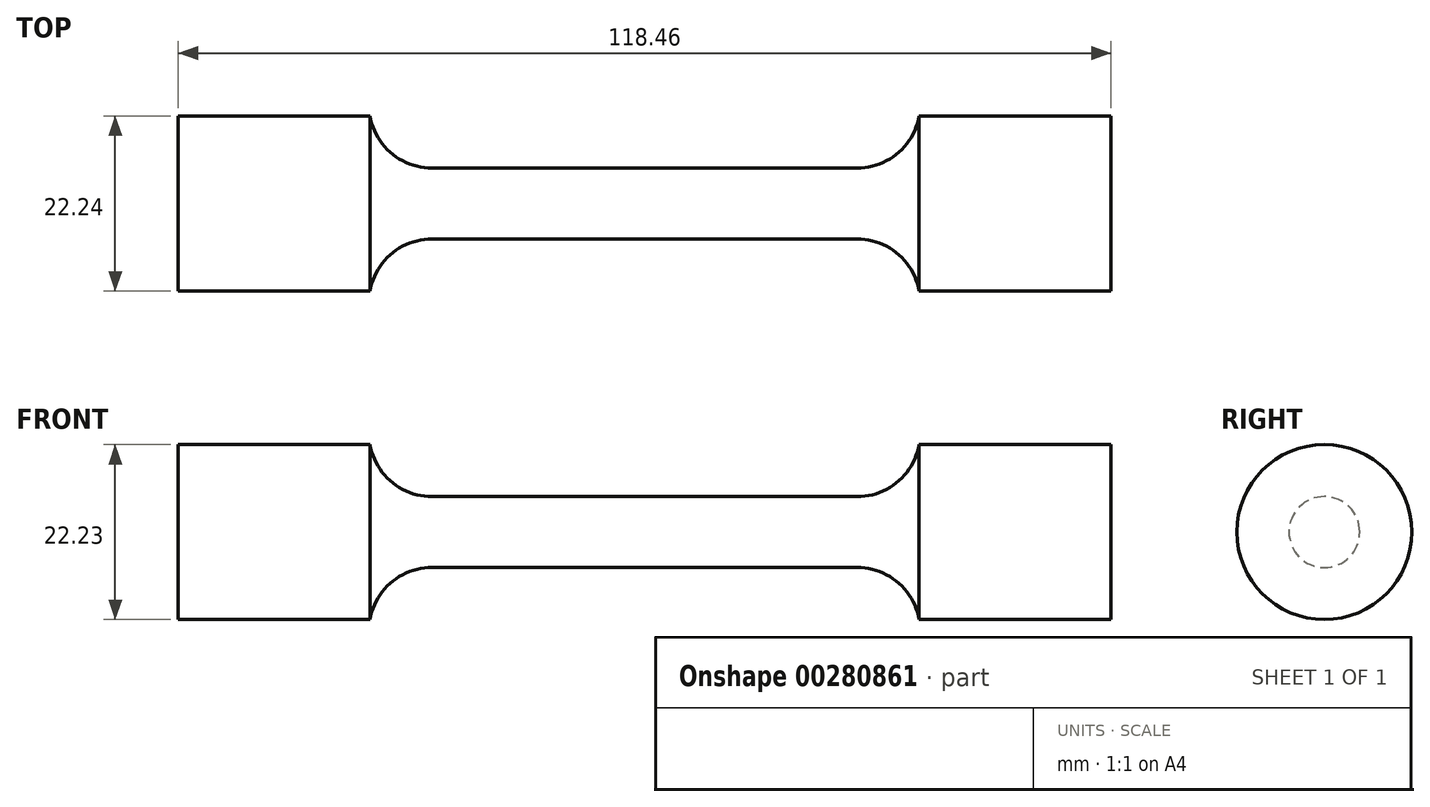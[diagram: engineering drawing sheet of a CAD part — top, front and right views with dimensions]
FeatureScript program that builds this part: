
annotation { "Feature Type Name" : "Feature", "Feature Type Description" : "" }
export const myFeature = defineFeature(function(context is Context, id is Id, definition is map)
    precondition{}
    {
        {
            var Q0;
            Q0=qCreatedBy(makeId("Front.planeOp"),FACE);
            var sketch = newSketch(context, id + "F0", { "sketchPlane" : qUnion([Q0])});
            skLineSegment(sketch, "E0", {"start": v(59.25, 4.51) * mm, "end": v(86.25, 4.51) * mm});
            skArc(sketch, "E1", {"start": v(86.25, 4.51) * mm, "mid": v(91.4, 6.39) * mm, "end": v(94.13, 11.13) * mm});
            skLineSegment(sketch, "E2", {"start": v(94.13, 11.13) * mm, "end": v(118.48, 11.13) * mm});
            skLineSegment(sketch, "E3", {"start": v(118.48, 11.13) * mm, "end": v(118.48, 0.01) * mm});
            skLineSegment(sketch, "E4.MirrorCS", {"start": v(59.25, 4.51) * mm, "end": v(32.25, 4.51) * mm});
            skLineSegment(sketch, "E5.MirrorCS", {"start": v(0.02, 11.13) * mm, "end": v(0.02, 0.01) * mm});
            skLineSegment(sketch, "E6.MirrorCS", {"start": v(24.37, 11.13) * mm, "end": v(0.02, 11.13) * mm});
            skArc(sketch, "E7.MirrorCS", {"start": v(32.25, 4.51) * mm, "mid": v(27.1, 6.39) * mm, "end": v(24.37, 11.13) * mm});
            skLineSegment(sketch, "E8", {"start": v(0.02, 0.01) * mm, "end": v(118.48, 0.01) * mm});
            skSolve(sketch);
        }
        {
            var Q0;
            Q0=makeQuery(id+"F0.imprint","IMPRINT",FACE,{"disambiguationData":[TD([[makeQuery(id+"F0.imprint","IMPRINT",EDGE,{"derivedFrom":sQuery(id+"F0.wireOp",EDGE,"E0")}),-1.0]])]});
            var Q1;
            Q1=sQuery(id+"F0.wireOp",EDGE,"E0");
            var Q2;
            Q2=sQuery(id+"F0.wireOp",EDGE,"E1");
            var Q3;
            Q3=sQuery(id+"F0.wireOp",EDGE,"E2");
            var Q4;
            Q4=sQuery(id+"F0.wireOp",EDGE,"E3");
            var Q5;
            Q5=sQuery(id+"F0.wireOp",EDGE,"E4.MirrorCS");
            var Q6;
            Q6=sQuery(id+"F0.wireOp",EDGE,"E5.MirrorCS");
            var Q7;
            Q7=sQuery(id+"F0.wireOp",EDGE,"E6.MirrorCS");
            var Q8;
            Q8=sQuery(id+"F0.wireOp",EDGE,"E7.MirrorCS");
            var Q9;
            Q9=sQuery(id+"F0.wireOp",EDGE,"E8");
            var Q10;
            Q10=sQuery(id+"F0.wireOp",EDGE,"E8");
            revolve(context, id + "F1", {"entities" : qUnion([Q0]), "surfaceEntities" : qUnion([Q1, Q2, Q3, Q4, Q5, Q6, Q7, Q8, Q9]), "axis" : qUnion([Q10]), "revolveType" : RevolveType.FULL});
        }
    });
